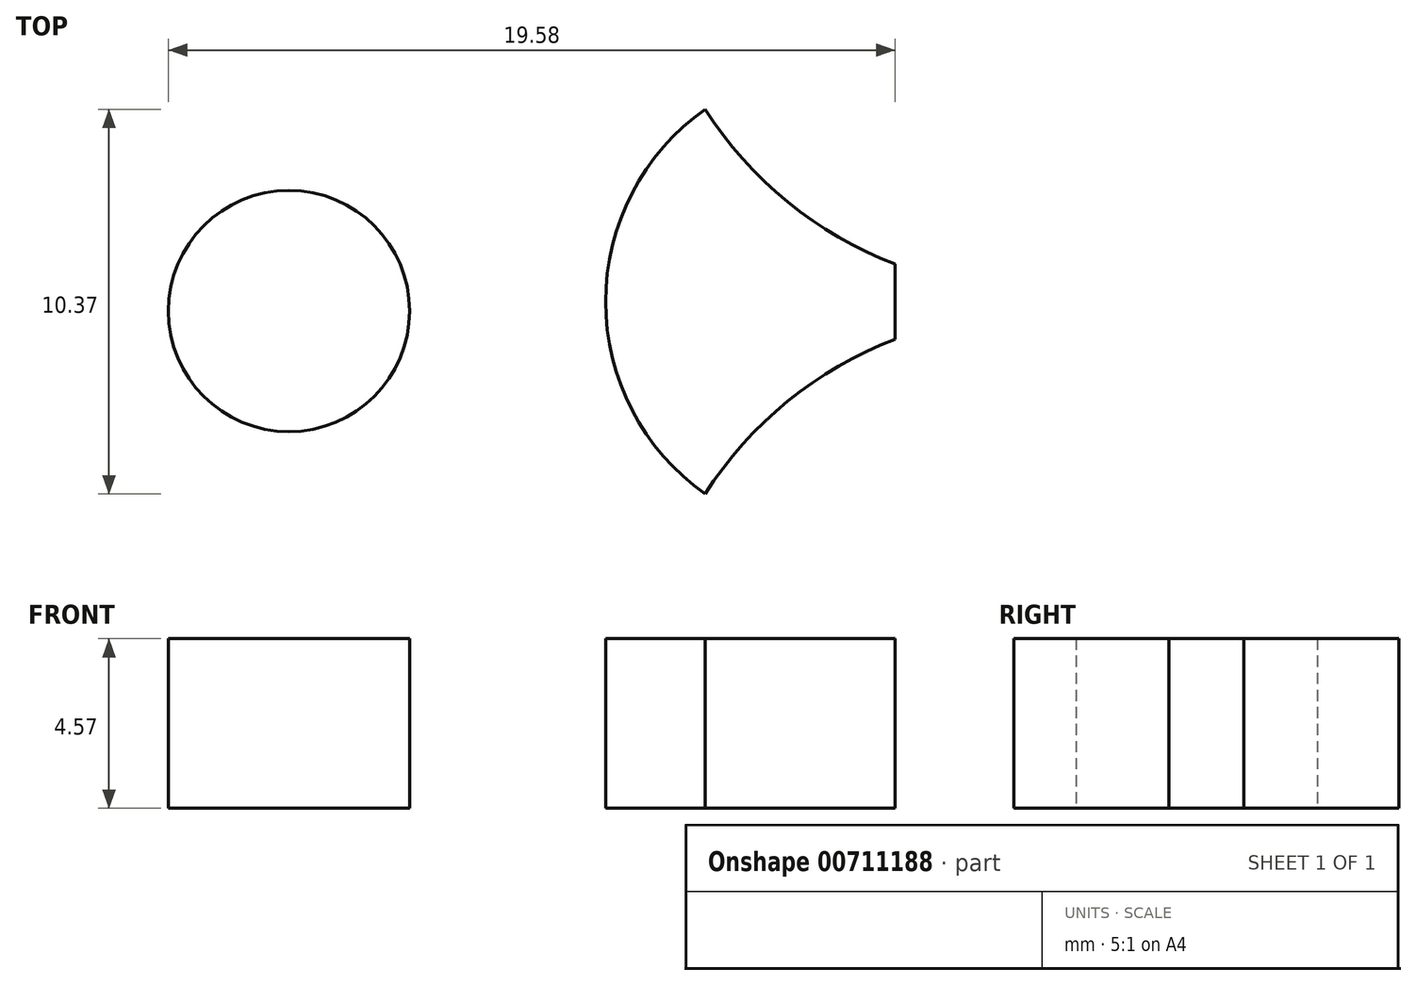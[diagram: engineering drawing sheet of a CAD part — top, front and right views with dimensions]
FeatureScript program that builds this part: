
annotation { "Feature Type Name" : "Feature", "Feature Type Description" : "" }
export const myFeature = defineFeature(function(context is Context, id is Id, definition is map)
    precondition{}
    {
        {
            var Q0;
            Q0=qCreatedBy(makeId("Top.planeOp"),FACE);
            var sketch = newSketch(context, id + "F0", { "sketchPlane" : qUnion([Q0])});
            skCircle(sketch, "E0", {"center": v(0.32, 0.06) * mm, "radius": 3.25 * mm});
            skArc(sketch, "E1", {"start": v(11.53, 5.5) * mm, "mid": v(13.76, 3) * mm, "end": v(16.65, 1.33) * mm});
            skLineSegment(sketch, "E2", {"start": v(16.65, 1.33) * mm, "end": v(16.65, 0.32) * mm});
            skArc(sketch, "E3.MirrorCS", {"start": v(11.53, -4.87) * mm, "mid": v(13.76, -2.37) * mm, "end": v(16.65, -0.7) * mm});
            skLineSegment(sketch, "E4", {"start": v(16.65, -0.7) * mm, "end": v(16.65, 0.32) * mm});
            skArc(sketch, "E5", {"start": v(11.53, 5.5) * mm, "mid": v(8.85, 0.32) * mm, "end": v(11.53, -4.87) * mm});
            skSolve(sketch);
        }
        {
            var Q0;
            Q0=makeQuery(id+"F0.imprint","IMPRINT",FACE,{"disambiguationData":[TD([[makeQuery(id+"F0.imprint","IMPRINT",EDGE,{"derivedFrom":sQuery(id+"F0.wireOp",EDGE,"E0")}),1.0]])]});
            var Q1;
            Q1=makeQuery(id+"F0.imprint","IMPRINT",FACE,{"disambiguationData":[TD([[makeQuery(id+"F0.imprint","IMPRINT",EDGE,{"derivedFrom":sQuery(id+"F0.wireOp",EDGE,"E1")}),-1.0]])]});
            extrude(context, id + "F1", {"entities" : qUnion([Q0, Q1]), "depth" : 4.57 * mm, "offsetDistance" : 25.4 * mm});
        }
    });
